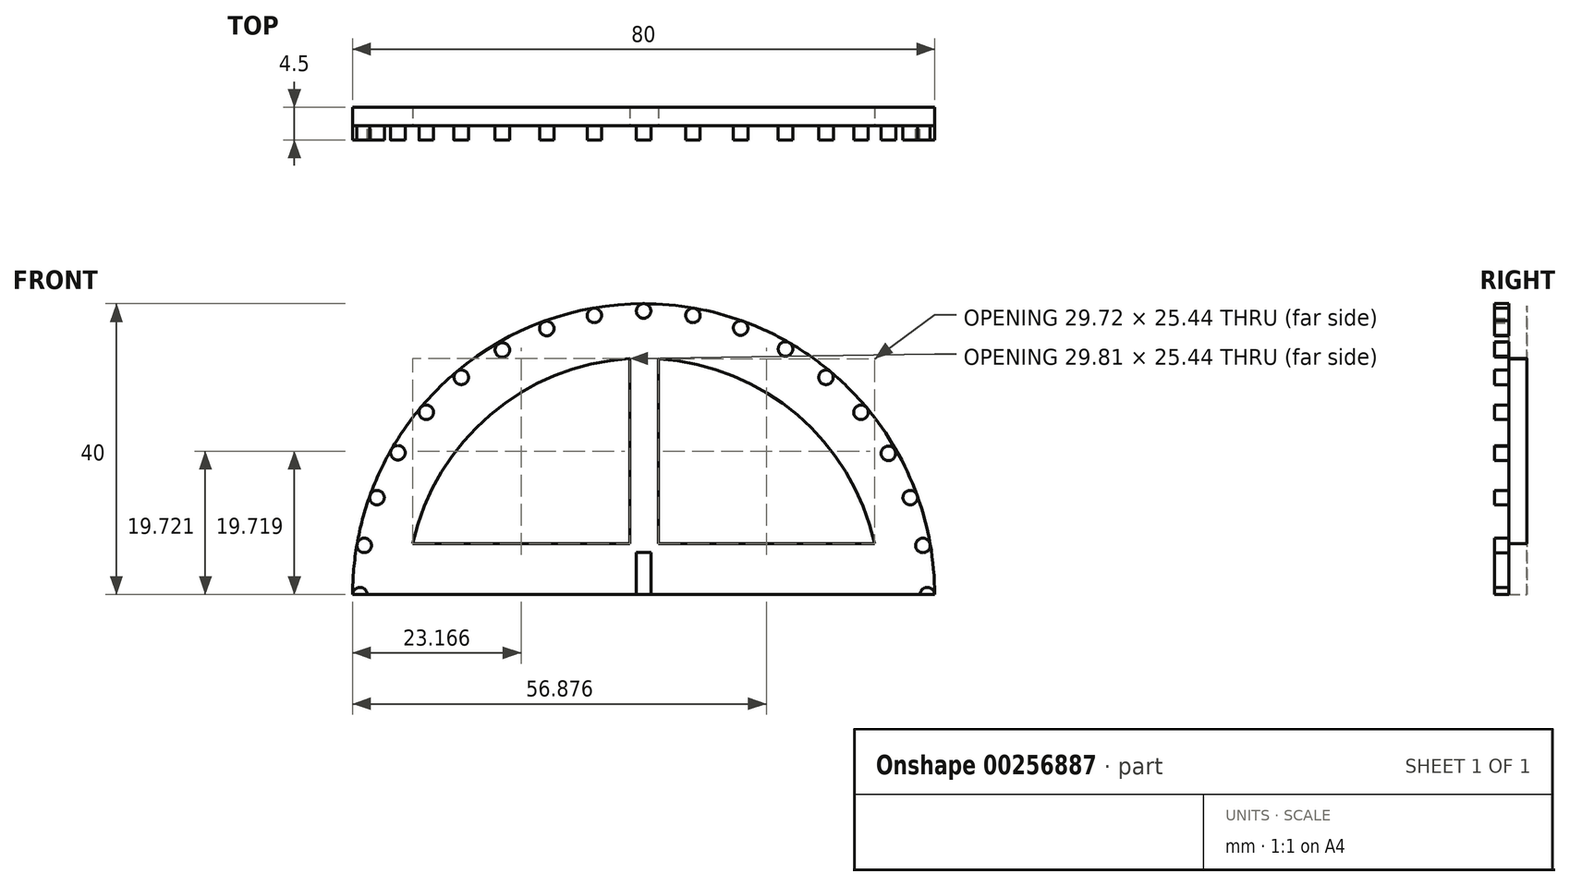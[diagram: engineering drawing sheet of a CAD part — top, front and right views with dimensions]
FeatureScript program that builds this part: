
annotation { "Feature Type Name" : "Feature", "Feature Type Description" : "" }
export const myFeature = defineFeature(function(context is Context, id is Id, definition is map)
    precondition{}
    {
        {
            var Q0;
            Q0=qCreatedBy(makeId("Front.planeOp"),FACE);
            var sketch = newSketch(context, id + "F0", { "sketchPlane" : qUnion([Q0])});
            skCircle(sketch, "E0", {"center": v(0, 0) * mm, "radius": 40 * mm});
            skLineSegment(sketch, "E1", {"start": v(0, 0) * mm, "end": v(-40, 0) * mm});
            skLineSegment(sketch, "E2", {"start": v(0, 0) * mm, "end": v(40, 0) * mm});
            skSolve(sketch);
        }
        {
            var Q0;
            Q0 = qSketchRegion(id + "F0", true);
            extrude(context, id + "F1", {"entities" : qUnion([Q0]), "depth" : 2.5 * mm});
        }
        {
            var Q0;
            Q0=makeQuery(id+"F1.opExtrude","CAP_FACE",FACE,{"disambiguationData":[OSD([sQuery(id+"F0.wireOp",EDGE,"E0")])],"isStart":false});
            var sketch = newSketch(context, id + "F2", { "sketchPlane" : qUnion([Q0])});
            skLineSegment(sketch, "E3.bottom", {"start": v(-43.47, 0) * mm, "end": v(48.23, 0) * mm});
            skLineSegment(sketch, "E3.top", {"start": v(-43.47, -45.4) * mm, "end": v(48.23, -45.4) * mm});
            skLineSegment(sketch, "E3.left", {"start": v(-43.47, 0) * mm, "end": v(-43.47, -45.4) * mm});
            skLineSegment(sketch, "E3.right", {"start": v(48.23, 0) * mm, "end": v(48.23, -45.4) * mm});
            skSolve(sketch);
        }
        {
            var Q0;
            Q0 = qSketchRegion(id + "F2", true);
            extrude(context, id + "F3", {"entities" : qUnion([Q0]), "operationType" : NewBodyOperationType.REMOVE, "oppositeDirection" : true, "depth" : 3 * mm});
        }
        {
            var Q0;
            Q0=makeQuery(id+"F1.opExtrude","CAP_FACE",FACE,{"disambiguationData":[OSD([sQuery(id+"F0.wireOp",EDGE,"E0")])],"isStart":false});
            var sketch = newSketch(context, id + "F4", { "sketchPlane" : qUnion([Q0])});
            skLineSegment(sketch, "E4", {"start": v(0, 0) * mm, "end": v(-39.4, 6.95) * mm});
            skCircle(sketch, "E5", {"center": v(-38.4, 6.77) * mm, "radius": 1 * mm});
            skLineSegment(sketch, "E6", {"start": v(0, 0) * mm, "end": v(-37.59, 13.68) * mm});
            skLineSegment(sketch, "E7", {"start": v(0, 0) * mm, "end": v(-34.64, 20) * mm});
            skLineSegment(sketch, "E8", {"start": v(0, 0) * mm, "end": v(-30.64, 25.71) * mm});
            skLineSegment(sketch, "E9", {"start": v(0, 0) * mm, "end": v(-25.71, 30.64) * mm});
            skLineSegment(sketch, "E10", {"start": v(0, 0) * mm, "end": v(-20, 34.64) * mm});
            skLineSegment(sketch, "E11", {"start": v(0, 0) * mm, "end": v(-13.68, 37.59) * mm});
            skLineSegment(sketch, "E12", {"start": v(0, 0) * mm, "end": v(-6.95, 39.4) * mm});
            skLineSegment(sketch, "E13", {"start": v(0, 0) * mm, "end": v(0, 40) * mm});
            skLineSegment(sketch, "E14", {"start": v(0, 0) * mm, "end": v(6.95, 39.4) * mm});
            skLineSegment(sketch, "E15", {"start": v(0, 0) * mm, "end": v(13.68, 37.59) * mm});
            skLineSegment(sketch, "E16", {"start": v(0, 0) * mm, "end": v(20, 34.64) * mm});
            skLineSegment(sketch, "E17", {"start": v(0, 0) * mm, "end": v(25.71, 30.64) * mm});
            skLineSegment(sketch, "E18", {"start": v(0, 0) * mm, "end": v(34.64, 20) * mm});
            skLineSegment(sketch, "E19", {"start": v(0, 0) * mm, "end": v(30.64, 25.71) * mm});
            skLineSegment(sketch, "E20", {"start": v(0, 0) * mm, "end": v(37.59, 13.68) * mm});
            skLineSegment(sketch, "E21", {"start": v(0, 0) * mm, "end": v(39.4, 6.95) * mm});
            skCircle(sketch, "E22", {"center": v(-36.65, 13.34) * mm, "radius": 1 * mm});
            skCircle(sketch, "E23", {"center": v(-33.77, 19.5) * mm, "radius": 1 * mm});
            skCircle(sketch, "E24", {"center": v(-29.88, 25.07) * mm, "radius": 1 * mm});
            skCircle(sketch, "E25", {"center": v(-25.07, 29.88) * mm, "radius": 1 * mm});
            skCircle(sketch, "E26", {"center": v(-19.42, 33.64) * mm, "radius": 1 * mm});
            skCircle(sketch, "E27", {"center": v(-13.32, 36.59) * mm, "radius": 1 * mm});
            skCircle(sketch, "E28", {"center": v(-6.77, 38.4) * mm, "radius": 1 * mm});
            skCircle(sketch, "E29", {"center": v(0, 39) * mm, "radius": 1 * mm});
            skCircle(sketch, "E30", {"center": v(6.77, 38.4) * mm, "radius": 1 * mm});
            skCircle(sketch, "E31", {"center": v(13.34, 36.65) * mm, "radius": 1 * mm});
            skCircle(sketch, "E32", {"center": v(19.5, 33.77) * mm, "radius": 1 * mm});
            skCircle(sketch, "E33", {"center": v(25.07, 29.88) * mm, "radius": 1 * mm});
            skCircle(sketch, "E34", {"center": v(29.88, 25.07) * mm, "radius": 1 * mm});
            skCircle(sketch, "E35", {"center": v(33.64, 19.42) * mm, "radius": 1 * mm});
            skCircle(sketch, "E36", {"center": v(36.65, 13.34) * mm, "radius": 1 * mm});
            skCircle(sketch, "E37", {"center": v(38.4, 6.77) * mm, "radius": 1 * mm});
            skCircle(sketch, "E38", {"center": v(39, 0) * mm, "radius": 1 * mm});
            skCircle(sketch, "E39", {"center": v(-39, 0) * mm, "radius": 1 * mm});
            skSolve(sketch);
        }
        {
            var Q0;
            Q0 = qSketchRegion(id + "F4", true);
            extrude(context, id + "F5", {"entities" : qUnion([Q0]), "operationType" : NewBodyOperationType.ADD, "depth" : 2 * mm});
        }
        {
            var Q0;
            Q0=makeQuery(id+"F1.opExtrude","CAP_FACE",FACE,{"disambiguationData":[OSD([sQuery(id+"F0.wireOp",EDGE,"E0")])],"isStart":false});
            var sketch = newSketch(context, id + "F6", { "sketchPlane" : qUnion([Q0])});
            skLineSegment(sketch, "E40.bottom", {"start": v(-1, 5.8) * mm, "end": v(1, 5.8) * mm});
            skLineSegment(sketch, "E40.top", {"start": v(-1, -5.8) * mm, "end": v(1, -5.8) * mm});
            skLineSegment(sketch, "E40.left", {"start": v(-1, 5.8) * mm, "end": v(-1, -5.8) * mm});
            skLineSegment(sketch, "E40.right", {"start": v(1, 5.8) * mm, "end": v(1, -5.8) * mm});
            skPoint(sketch, "E40.middle", {"position": v(0, 0) * mm});
            skSolve(sketch);
        }
        {
            var Q0;
            Q0 = qSketchRegion(id + "F6", true);
            extrude(context, id + "F7", {"entities" : qUnion([Q0]), "operationType" : NewBodyOperationType.ADD, "depth" : 2 * mm});
        }
        {
            var Q0;
            Q0=makeQuery(id+"F1.opExtrude","CAP_FACE",FACE,{"disambiguationData":[OSD([sQuery(id+"F0.wireOp",EDGE,"E0")])],"isStart":false});
            var sketch = newSketch(context, id + "F8", { "sketchPlane" : qUnion([Q0])});
            skLineSegment(sketch, "E41.bottom", {"start": v(-42.4, 0) * mm, "end": v(42.73, 0) * mm});
            skLineSegment(sketch, "E41.top", {"start": v(-42.4, -8.42) * mm, "end": v(42.73, -8.42) * mm});
            skLineSegment(sketch, "E41.left", {"start": v(-42.4, 0) * mm, "end": v(-42.4, -8.42) * mm});
            skLineSegment(sketch, "E41.right", {"start": v(42.73, 0) * mm, "end": v(42.73, -8.42) * mm});
            skSolve(sketch);
        }
        {
            var Q0;
            Q0 = qSketchRegion(id + "F8", true);
            extrude(context, id + "F9", {"entities" : qUnion([Q0]), "operationType" : NewBodyOperationType.REMOVE, "depth" : 25 * mm});
        }
        {
            var Q0;
            Q0=makeQuery(id+"F1.opExtrude","CAP_FACE",FACE,{"disambiguationData":[OSD([sQuery(id+"F0.wireOp",EDGE,"E0")])],"isStart":false});
            var sketch = newSketch(context, id + "F10", { "sketchPlane" : qUnion([Q0])});
            skCircle(sketch, "E42", {"center": v(0, 0) * mm, "radius": 32.5 * mm});
            skLineSegment(sketch, "E43", {"start": v(-1.93, 32.44) * mm, "end": v(-1.93, 7) * mm});
            skLineSegment(sketch, "E44", {"start": v(-1.93, 7) * mm, "end": v(-31.74, 7) * mm});
            skLineSegment(sketch, "E45", {"start": v(2.01, 7) * mm, "end": v(2.01, 32.44) * mm});
            skLineSegment(sketch, "E46.bottom", {"start": v(2.01, 7) * mm, "end": v(31.74, 7) * mm});
            skLineSegment(sketch, "E46.top", {"start": v(2.01, 7) * mm, "end": v(31.74, 7) * mm});
            skLineSegment(sketch, "E46.left", {"start": v(2.01, 7) * mm, "end": v(2.01, 7) * mm});
            skLineSegment(sketch, "E46.right", {"start": v(31.74, 7) * mm, "end": v(31.74, 7) * mm});
            skSolve(sketch);
        }
        {
            var Q0;
            {var subQ0=sQuery(id+"F10.wireOp",EDGE,"E43");Q0=makeQuery(id+"F10.imprint","IMPRINT",FACE,{"disambiguationData":[TD([[makeQuery(id+"F10.imprint","IMPRINT",EDGE,{"derivedFrom":subQ0}),-1.0]])]});}
            var Q1;
            {var subQ0=sQuery(id+"F10.wireOp",EDGE,"E45");Q1=makeQuery(id+"F10.imprint","IMPRINT",FACE,{"disambiguationData":[TD([[makeQuery(id+"F10.imprint","IMPRINT",EDGE,{"derivedFrom":subQ0}),-1.0]])]});}
            extrude(context, id + "F11", {"entities" : qUnion([Q0, Q1]), "operationType" : NewBodyOperationType.REMOVE, "oppositeDirection" : true, "depth" : 25 * mm});
        }
    });
